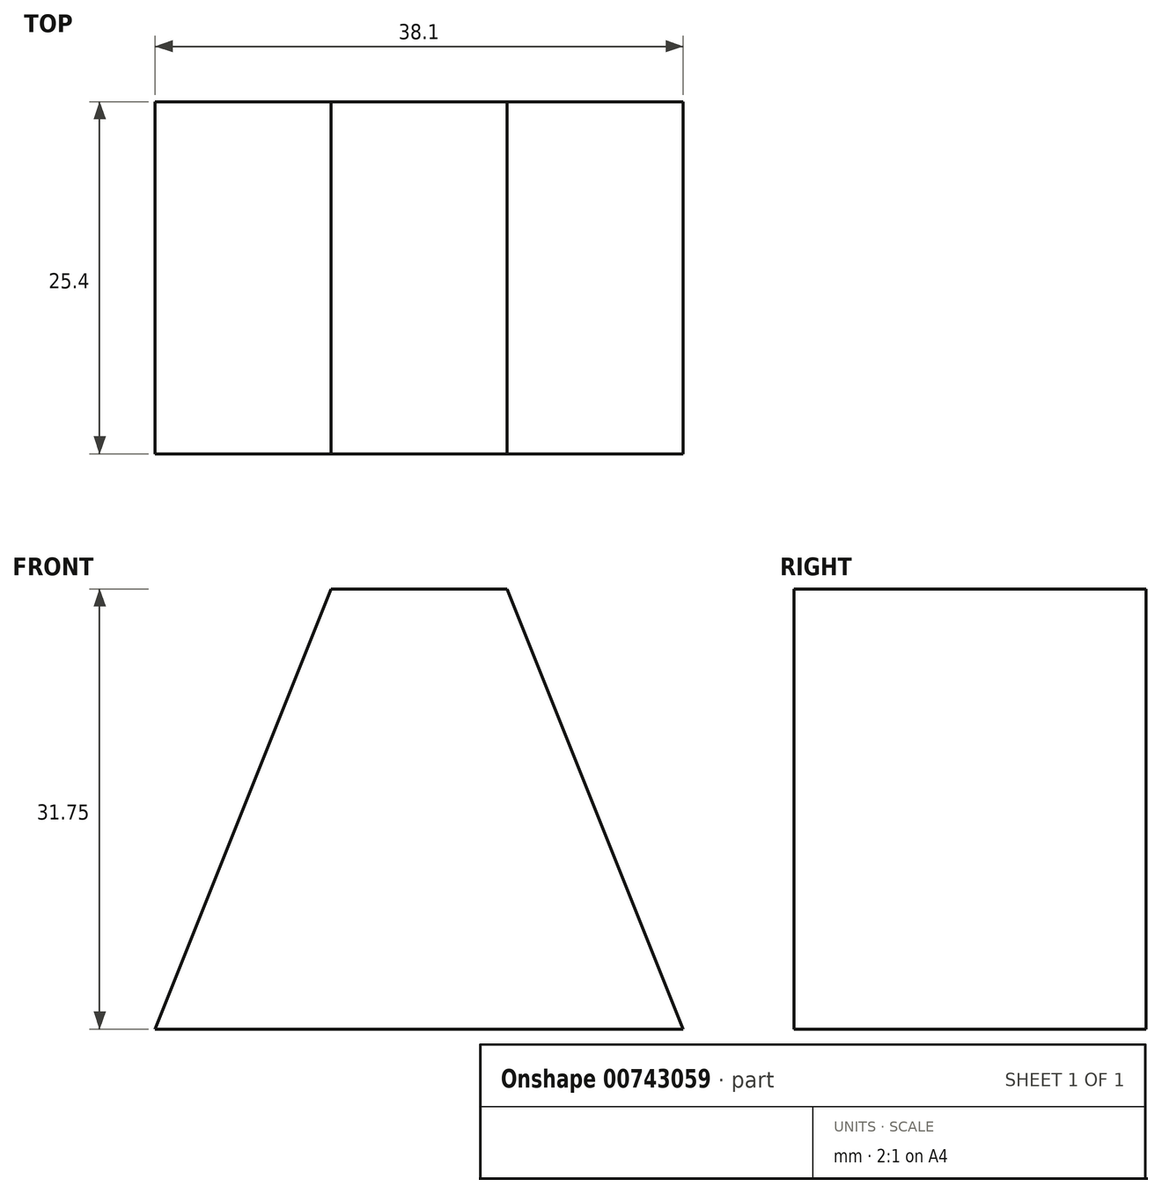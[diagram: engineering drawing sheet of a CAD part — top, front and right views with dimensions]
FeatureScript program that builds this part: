
annotation { "Feature Type Name" : "Feature", "Feature Type Description" : "" }
export const myFeature = defineFeature(function(context is Context, id is Id, definition is map)
    precondition{}
    {
        {
            var Q0;
            Q0=qCreatedBy(makeId("Front.planeOp"),FACE);
            var sketch = newSketch(context, id + "F0", { "sketchPlane" : qUnion([Q0])});
            skLineSegment(sketch, "E0", {"start": v(0, 0) * mm, "end": v(38.1, 0) * mm});
            skLineSegment(sketch, "E1", {"start": v(38.1, 0) * mm, "end": v(38.1, 31.75) * mm});
            skLineSegment(sketch, "E2", {"start": v(38.1, 31.75) * mm, "end": v(0, 31.75) * mm});
            skLineSegment(sketch, "E3", {"start": v(0, 31.75) * mm, "end": v(0, 0) * mm});
            skLineSegment(sketch, "E4", {"start": v(0, 0) * mm, "end": v(12.7, 31.75) * mm});
            skLineSegment(sketch, "E5", {"start": v(12.7, 31.75) * mm, "end": v(0, 31.75) * mm});
            skLineSegment(sketch, "E6", {"start": v(38.1, 0) * mm, "end": v(25.4, 31.75) * mm});
            skLineSegment(sketch, "E7", {"start": v(25.4, 31.75) * mm, "end": v(38.1, 31.75) * mm});
            skLineSegment(sketch, "E8", {"start": v(38.1, 31.75) * mm, "end": v(38.1, 0) * mm});
            skSolve(sketch);
        }
        {
            var Q0;
            Q0=makeQuery(id+"F0.imprint","IMPRINT",FACE,{"disambiguationData":[TD([[makeQuery(id+"F0.imprint","IMPRINT",EDGE,{"derivedFrom":sQuery(id+"F0.wireOp",EDGE,"E0")}),1.0]])]});
            extrude(context, id + "F1", {"entities" : qUnion([Q0]), "oppositeDirection" : true, "depth" : 25.4 * mm, "offsetDistance" : 25.4 * mm});
        }
    });
